# Revit family: 482066001(1)
name_source: partatom
category: Generic Models
units: mm (PartAtom-declared; Revit-internal decimal feet)

## family parameters
Always vertical = Yes
Can host rebar = No
Cut with Voids When Loaded = No
Host = Floor
Room Calculation Point = No
Shared = Yes

## types (1)
- 482066001
    ARTICLENO = NB
    BEZ = Zonder rooster, met loodslap 33 x 33cm, 15 ponds (=ca. 1,3 mm dik), Stortkoker Ø 90 mm
    BOMINFO = LINA
    CATALOG = König & Ronneberger
    CNSORDERNO = 482066001
    D = 108 mm  [stored 0.354331 ft]
    D1 = 94 mm  [stored 0.308399 ft]
    D2 = 0 mm  [stored 0 ft]
    Description = Balcony transit and drain wastes
    H = 0 mm  [stored 0 ft]
    H1 = 95 mm  [stored 0.31168 ft]
    HTML = Product page
    INFO = PDF Catalog
    LINA = 482066001
    LODLEVEL = 300
    Manufacturer = KOERO
    Model = 482066001
    NB = 482066001(1)
    NBSYN = $CNSORDERNO.($LODLEVEL.)
    NN = PLUVETTA®MET LODEN SLAB
    NT = Balcony transit and drain wastes
    SUPPLIER = KOERO

note: [stored X ft] marks values corroborated as IEEE doubles in the binary element streams (Revit-internal decimal feet)

## geometry (parser evidence)
native form markers: Sweep x4
no freeform markers — native parametric forms only
